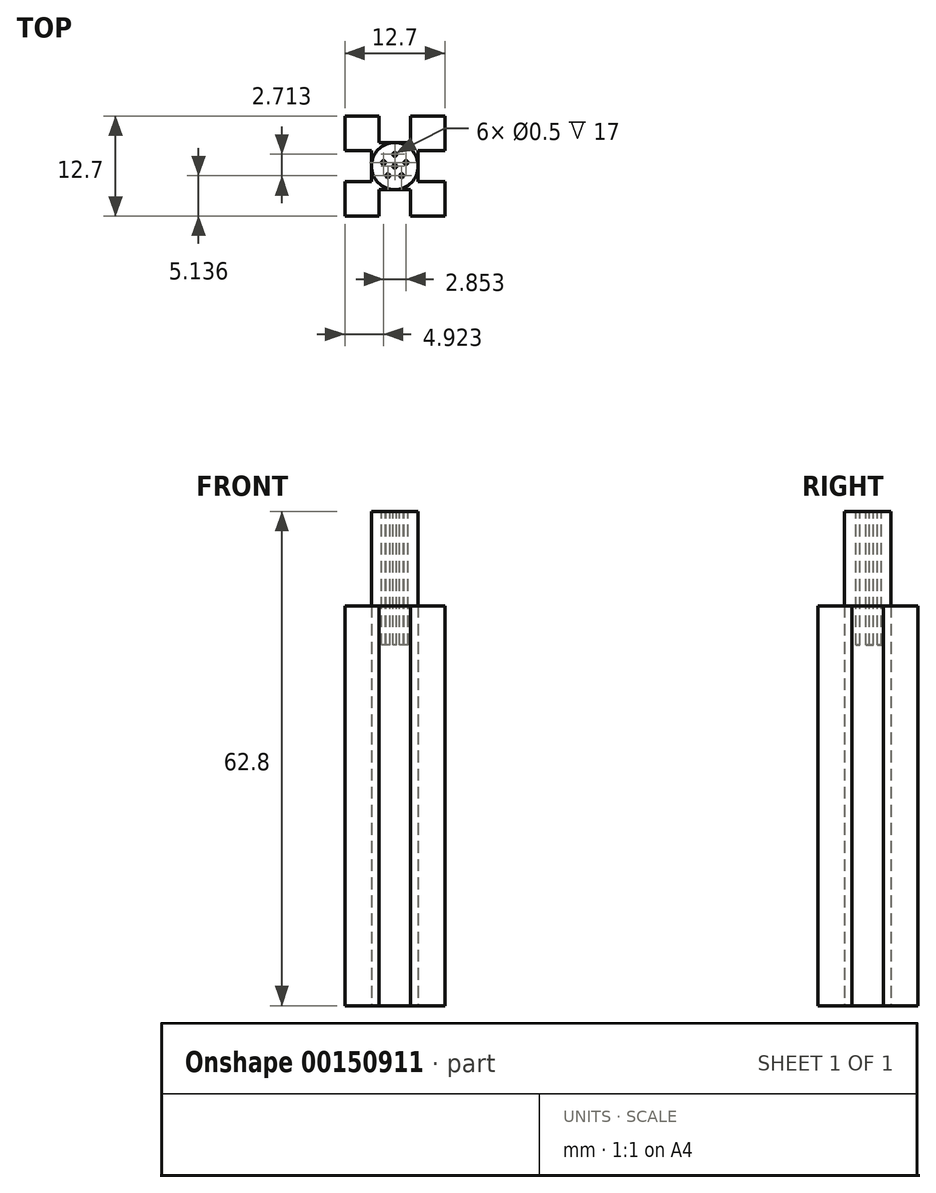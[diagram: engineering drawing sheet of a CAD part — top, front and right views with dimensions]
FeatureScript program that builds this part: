
annotation { "Feature Type Name" : "Feature", "Feature Type Description" : "" }
export const myFeature = defineFeature(function(context is Context, id is Id, definition is map)
    precondition{}
    {
        {
            var Q0;
            Q0=qCreatedBy(makeId("Top.planeOp"),FACE);
            var sketch = newSketch(context, id + "F0", { "sketchPlane" : qUnion([Q0])});
            skLineSegment(sketch, "E0.bottom", {"start": v(-6.35, 6.35) * mm, "end": v(-1.99, 6.35) * mm});
            skLineSegment(sketch, "E0.top", {"start": v(-6.35, -6.35) * mm, "end": v(-1.99, -6.35) * mm});
            skLineSegment(sketch, "E0.left", {"start": v(-6.35, 6.35) * mm, "end": v(-6.35, 1.99) * mm});
            skLineSegment(sketch, "E0.right", {"start": v(6.35, 6.35) * mm, "end": v(6.35, 1.99) * mm});
            skLineSegment(sketch, "E1", {"start": v(-6.35, 6.35) * mm, "end": v(6.35, -6.35) * mm, "construction": true});
            skLineSegment(sketch, "E2.top", {"start": v(-1.99, 2.97) * mm, "end": v(1.99, 2.97) * mm});
            skLineSegment(sketch, "E2.left", {"start": v(-1.99, 6.35) * mm, "end": v(-1.99, 2.97) * mm});
            skLineSegment(sketch, "E2.right", {"start": v(1.99, 6.35) * mm, "end": v(1.99, 2.97) * mm});
            skLineSegment(sketch, "E3.bottom", {"start": v(6.35, 1.99) * mm, "end": v(2.98, 1.99) * mm});
            skLineSegment(sketch, "E3.top", {"start": v(6.35, -1.99) * mm, "end": v(2.98, -1.99) * mm});
            skLineSegment(sketch, "E3.right", {"start": v(2.98, 1.99) * mm, "end": v(2.98, -1.99) * mm});
            skLineSegment(sketch, "E4.top", {"start": v(-1.99, -2.98) * mm, "end": v(1.99, -2.98) * mm});
            skLineSegment(sketch, "E4.left", {"start": v(-1.99, -6.35) * mm, "end": v(-1.99, -2.98) * mm});
            skLineSegment(sketch, "E4.right", {"start": v(1.99, -6.35) * mm, "end": v(1.99, -2.98) * mm});
            skLineSegment(sketch, "E5.bottom", {"start": v(-6.35, -1.99) * mm, "end": v(-2.98, -1.99) * mm});
            skLineSegment(sketch, "E5.top", {"start": v(-6.35, 1.99) * mm, "end": v(-2.98, 1.99) * mm});
            skLineSegment(sketch, "E5.right", {"start": v(-2.98, -1.99) * mm, "end": v(-2.98, 1.99) * mm});
            skLineSegment(sketch, "E6.trimOffspring", {"start": v(-6.35, -1.99) * mm, "end": v(-6.35, -6.35) * mm});
            skLineSegment(sketch, "E7.trimOffspring", {"start": v(1.99, 6.35) * mm, "end": v(6.35, 6.35) * mm});
            skLineSegment(sketch, "E8.trimOffspring", {"start": v(6.35, -1.99) * mm, "end": v(6.35, -6.35) * mm});
            skLineSegment(sketch, "E9.trimOffspring", {"start": v(1.99, -6.35) * mm, "end": v(6.35, -6.35) * mm});
            skPoint(sketch, "E10", {"position": v(0, 0) * mm});
            skSolve(sketch);
        }
        {
            var Q0;
            Q0=qSketchRegion(id+"F0",true);
            extrude(context, id + "F1", {"entities" : qUnion([Q0]), "depth" : 50.8 * mm});
        }
        {
            var Q0;
            Q0=makeQuery(id+"F1.opExtrude","CAP_FACE",FACE,{"disambiguationData":[OSD([sQuery(id+"F0.wireOp",EDGE,"E0.bottom"),sQuery(id+"F0.wireOp",EDGE,"E0.top"),sQuery(id+"F0.wireOp",EDGE,"E0.left"),sQuery(id+"F0.wireOp",EDGE,"E0.right"),sQuery(id+"F0.wireOp",EDGE,"E2.top"),sQuery(id+"F0.wireOp",EDGE,"E2.left"),sQuery(id+"F0.wireOp",EDGE,"E2.right"),sQuery(id+"F0.wireOp",EDGE,"E3.bottom"),sQuery(id+"F0.wireOp",EDGE,"E3.top"),sQuery(id+"F0.wireOp",EDGE,"E3.right"),sQuery(id+"F0.wireOp",EDGE,"E4.top"),sQuery(id+"F0.wireOp",EDGE,"E4.left"),sQuery(id+"F0.wireOp",EDGE,"E4.right"),sQuery(id+"F0.wireOp",EDGE,"E5.bottom"),sQuery(id+"F0.wireOp",EDGE,"E5.top"),sQuery(id+"F0.wireOp",EDGE,"E5.right"),sQuery(id+"F0.wireOp",EDGE,"E6.trimOffspring"),sQuery(id+"F0.wireOp",EDGE,"E7.trimOffspring"),sQuery(id+"F0.wireOp",EDGE,"E8.trimOffspring"),sQuery(id+"F0.wireOp",EDGE,"E9.trimOffspring")])],"isStart":false});
            var sketch = newSketch(context, id + "F2", { "sketchPlane" : qUnion([Q0])});
            skCircle(sketch, "E11", {"center": v(0, 0) * mm, "radius": 2.98 * mm});
            skSolve(sketch);
        }
        {
            var Q0;
            Q0=qSketchRegion(id+"F2",true);
            extrude(context, id + "F3", {"entities" : qUnion([Q0]), "operationType" : NewBodyOperationType.ADD, "depth" : 12 * mm});
        }
        {
            var Q0;
            Q0=makeQuery(id+"F3.opExtrude","CAP_FACE",FACE,{"disambiguationData":[OSD([sQuery(id+"F2.wireOp",EDGE,"E11")])],"isStart":false});
            var sketch = newSketch(context, id + "F4", { "sketchPlane" : qUnion([Q0])});
            skCircle(sketch, "E12", {"center": v(0, 1.5) * mm, "radius": 0.25 * mm});
            skCircle(sketch, "E13.1.0", {"center": v(-1.43, 0.46) * mm, "radius": 0.25 * mm});
            skCircle(sketch, "E13.2.0", {"center": v(-0.88, -1.21) * mm, "radius": 0.25 * mm});
            skCircle(sketch, "E13.3.0", {"center": v(0.88, -1.21) * mm, "radius": 0.25 * mm});
            skPoint(sketch, "E13.center", {"position": v(0, 0) * mm});
            skCircle(sketch, "E14", {"center": v(0, 0) * mm, "radius": 0.25 * mm});
            skCircle(sketch, "E15.1.4.0", {"center": v(1.43, 0.46) * mm, "radius": 0.25 * mm});
            skSolve(sketch);
        }
        {
            var Q0;
            Q0 = qSketchRegion(id + "F4", true);
            extrude(context, id + "F5", {"entities" : qUnion([Q0]), "operationType" : NewBodyOperationType.REMOVE, "oppositeDirection" : true, "depth" : 17 * mm});
        }
    });
